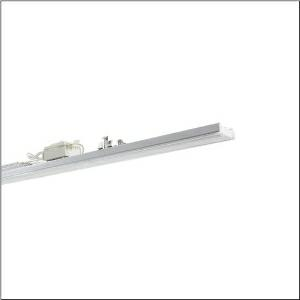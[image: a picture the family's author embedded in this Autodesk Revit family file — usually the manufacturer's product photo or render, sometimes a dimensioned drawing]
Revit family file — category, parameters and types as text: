
# Revit family: licross_11_recessed_ho_51tl12dv4b5m
name_source: partatom
category: Lighting Fixtures
units: mm (PartAtom-declared; Revit-internal decimal feet)

## family parameters
Cut with Voids When Loaded = No
Host = Face
Light Source = No
Part Type = Normal
Room Calculation Point = No
Round Connector Dimension = Use Diameter
Shared = No

## types (1)
- --- (1 x LED, 11630 lm, 59.3 W, 4000K)
    Apparent Load = 59 VA
    CIE Flux Codes = 66 91 98 100 100
    Color Rendering = 80
    Color Temperature = 4000K
    Default Elevation = 1800 mm
    Description = Licross 11 Recessed HO, luminaire insert, of sheet steel, coil coated, white, length: 2.250mm, width: 66mm, height: 67mm, LED rated luminous flux: 11.630lm, light colour: 840, SDCM (Standard Deviation of Colour Matching)MacAdam ≤ 2 SDCM (initial), control gear: DALI 2, with plug, 5-pole, with phase selection, mains connection: 220..240V, AC, 50/60Hz, rated input power: 59W, internal wiring halogen-free, primary optical cover: cover, of PMMA, light emission: direct distribution, primary light characteristic: symmetric, protection rating (complete): IP40, insulation class (complete): insulation class I (protective earthing), certification: CE, ENEC, VDE, UKCA, protection symbol: D if used in an environment without relevant dust loads with corresponding accessories, impact resistance: IK06, permissible ambient temperature for indoor applications: -25..+35°C, corresponds to IFS (International Featured Standards) requirements for safety and quality in the food industry, reducing of maximum allowable ambient temperature of 5°C with ceiling mounting, LABS conformity tested according to VDMA 24364:2018-05, The light source and the operating device comply with the requirements of the Ecodesign Regulation (EU) 2019/2020 and are replaceable in accordance with this regulation, packaging unit: 1 piece
    Height = 58 mm
    Lamp = 1 x LED
    Lamp Light Flux = 11630 lm
    Lamp Power = 59.3 W
    Lamp count = 1
    Length = 2250 mm
    Luminous efficacy = 196 lm/W
    Manufacturer = Siteco
    ModVariant = No
    Model = 51TL12DV4B5M
    Mounting Place = Ceiling
    Mounting Type = Pendant
    Number of Poles = 1
    OnlyDefault = Yes
    Power Factor = 1
    Product Name = Licross 11 Recessed HO
    Product group = luminaire insert | ceiling pendant
    ProductGroupID = 901
    Protection Class = Protection class I
    Protection Degree = IP 40
    RLX_Detail_Level = 1
    RLX_Emergency_Light_Flux = 0 lm
    RLX_Emergency_Type = 0
    RLX_Emergency_Type_DB = No
    RlxData = <blob elided: 29321 chars, md5=7766e5aa>
    Socket = socket
    Standby Power = 0 W
    System Light Flux = 11630 lm
    System Power = 59 W
    Type Comments = factory setting: luminous flux: 100 % | dim-lin: 254 | 278 mA
    Type Image = l_1296930.jpg
    URL = http://relux.com
    VarID = @adj_101191
    Voltage = 0 V
    Weight = 0.00 kg
    Width = 66 mm

## geometry (parser evidence)
native form markers: Blend x4, Sweep x9
no freeform markers — native parametric forms only
